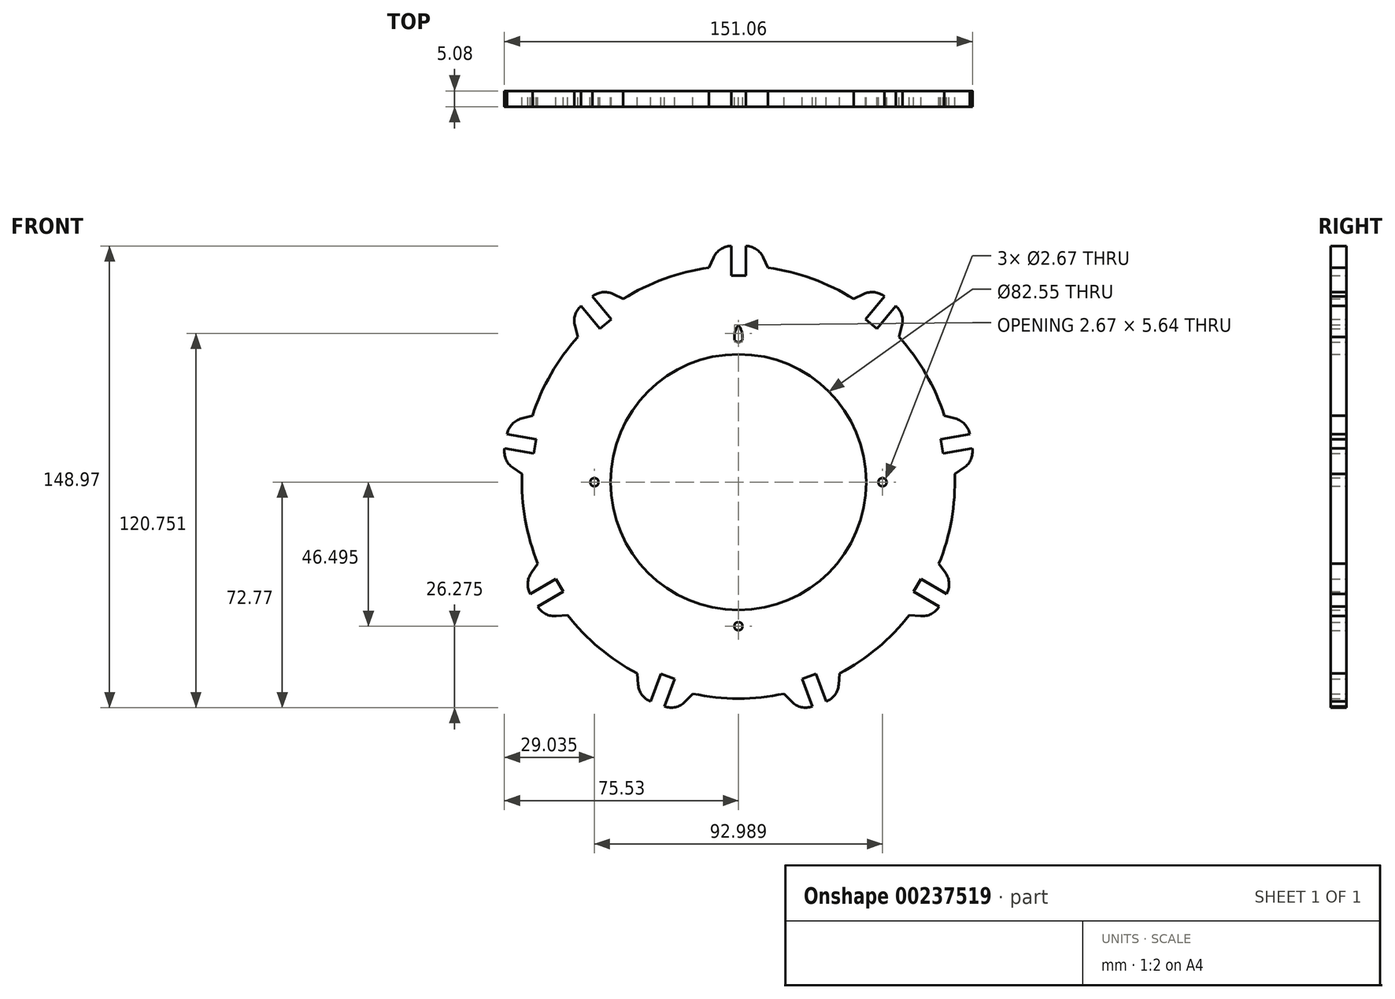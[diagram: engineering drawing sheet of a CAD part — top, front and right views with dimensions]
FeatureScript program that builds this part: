
annotation { "Feature Type Name" : "Feature", "Feature Type Description" : "" }
export const myFeature = defineFeature(function(context is Context, id is Id, definition is map)
    precondition{}
    {
        {
            var Q0;
            Q0=qCreatedBy(makeId("Front.planeOp"),FACE);
            var sketch = newSketch(context, id + "F0", { "sketchPlane" : qUnion([Q0])});
            skCircle(sketch, "E0", {"center": v(0, 0) * mm, "radius": 69.85 * mm});
            skCircle(sketch, "E1", {"center": v(0, 0) * mm, "radius": 41.28 * mm});
            skCircle(sketch, "E2", {"center": v(0, 0) * mm, "radius": 46.5 * mm, "construction": true});
            skPoint(sketch, "E3.center", {"position": v(0, -7.07) * mm});
            skLineSegment(sketch, "E4", {"start": v(-9.56, 69.2) * mm, "end": v(-8.05, 72.5) * mm});
            skLineSegment(sketch, "E5", {"start": v(-2.28, 76.2) * mm, "end": v(2.28, 76.2) * mm});
            skLineSegment(sketch, "E6", {"start": v(8.05, 72.5) * mm, "end": v(9.56, 69.2) * mm});
            skPoint(sketch, "E7", {"position": v(0, 76.2) * mm});
            skLineSegment(sketch, "E8", {"start": v(-9.56, 69.2) * mm, "end": v(-41.28, 0) * mm, "construction": true});
            skLineSegment(sketch, "E9", {"start": v(41.28, 0) * mm, "end": v(9.56, 69.2) * mm, "construction": true});
            skLineSegment(sketch, "E10", {"start": v(-2.35, 76.2) * mm, "end": v(-2.35, 66.67) * mm});
            skLineSegment(sketch, "E11", {"start": v(-2.35, 66.68) * mm, "end": v(2.35, 66.68) * mm});
            skLineSegment(sketch, "E12", {"start": v(2.35, 66.67) * mm, "end": v(2.35, 76.2) * mm});
            skPoint(sketch, "E13", {"position": v(0, 66.67) * mm});
            skPoint(sketch, "E14.visualSharp", {"position": v(-6.35, 76.2) * mm});
            skArc(sketch, "E14.filletArc", {"start": v(-2.28, 76.2) * mm, "mid": v(-5.7, 75.2) * mm, "end": v(-8.05, 72.5) * mm});
            skPoint(sketch, "E15.visualSharp", {"position": v(6.35, 76.2) * mm});
            skArc(sketch, "E15.filletArc", {"start": v(8.05, 72.5) * mm, "mid": v(5.7, 75.2) * mm, "end": v(2.28, 76.2) * mm});
            skCircle(sketch, "E16.MirrorC", {"center": v(0, 46.5) * mm, "radius": 1.33 * mm});
            skCircle(sketch, "E17", {"center": v(0, 0) * mm, "radius": 66.72 * mm, "construction": true});
            skCircle(sketch, "E18.1.0", {"center": v(-46.5, 0) * mm, "radius": 1.33 * mm});
            skCircle(sketch, "E18.2.0", {"center": v(0, -46.5) * mm, "radius": 1.33 * mm});
            skCircle(sketch, "E18.3.0", {"center": v(46.5, 0) * mm, "radius": 1.33 * mm});
            skCircle(sketch, "E19", {"center": v(0, 0) * mm, "radius": 50.8 * mm, "construction": true});
            skArc(sketch, "E20", {"start": v(1.33, 46.48) * mm, "mid": v(1, 48.74) * mm, "end": v(0, 50.8) * mm});
            skArc(sketch, "E21", {"start": v(0, 50.8) * mm, "mid": v(-1, 48.74) * mm, "end": v(-1.33, 46.48) * mm});
            skLineSegment(sketch, "E22.1.0", {"start": v(-51.8, 46.86) * mm, "end": v(-52.76, 50.36) * mm});
            skArc(sketch, "E22.1.1", {"start": v(-50.72, 56.91) * mm, "mid": v(-52.7, 53.94) * mm, "end": v(-52.76, 50.36) * mm});
            skLineSegment(sketch, "E22.1.2", {"start": v(-50.78, 56.86) * mm, "end": v(-44.66, 49.57) * mm});
            skLineSegment(sketch, "E22.1.3", {"start": v(-41.06, 52.59) * mm, "end": v(-47.18, 59.88) * mm});
            skArc(sketch, "E22.1.4", {"start": v(-40.43, 60.7) * mm, "mid": v(-43.96, 61.27) * mm, "end": v(-47.24, 59.84) * mm});
            skLineSegment(sketch, "E22.1.5", {"start": v(-40.43, 60.7) * mm, "end": v(-37.15, 59.15) * mm});
            skLineSegment(sketch, "E22.1.6", {"start": v(-44.66, 49.57) * mm, "end": v(-41.06, 52.59) * mm});
            skLineSegment(sketch, "E22.2.0", {"start": v(-69.8, 2.6) * mm, "end": v(-72.8, 4.66) * mm});
            skArc(sketch, "E22.2.1", {"start": v(-75.44, 11) * mm, "mid": v(-75.04, 7.44) * mm, "end": v(-72.8, 4.66) * mm});
            skLineSegment(sketch, "E22.2.2", {"start": v(-75.45, 10.92) * mm, "end": v(-66.07, 9.26) * mm});
            skLineSegment(sketch, "E22.2.3", {"start": v(-65.25, 13.9) * mm, "end": v(-74.63, 15.55) * mm});
            skArc(sketch, "E22.2.4", {"start": v(-70, 20.51) * mm, "mid": v(-73.06, 18.68) * mm, "end": v(-74.65, 15.47) * mm});
            skLineSegment(sketch, "E22.2.5", {"start": v(-70, 20.51) * mm, "end": v(-66.48, 21.43) * mm});
            skLineSegment(sketch, "E22.2.6", {"start": v(-66.07, 9.26) * mm, "end": v(-65.25, 13.9) * mm});
            skLineSegment(sketch, "E22.3.0", {"start": v(-55.14, -42.88) * mm, "end": v(-58.76, -43.22) * mm});
            skArc(sketch, "E22.3.1", {"start": v(-64.85, -40.07) * mm, "mid": v(-62.27, -42.54) * mm, "end": v(-58.76, -43.22) * mm});
            skLineSegment(sketch, "E22.3.2", {"start": v(-64.82, -40.13) * mm, "end": v(-56.57, -35.37) * mm});
            skLineSegment(sketch, "E22.3.3", {"start": v(-58.92, -31.3) * mm, "end": v(-67.17, -36.07) * mm});
            skArc(sketch, "E22.3.4", {"start": v(-66.8, -29.28) * mm, "mid": v(-67.97, -32.66) * mm, "end": v(-67.13, -36.13) * mm});
            skLineSegment(sketch, "E22.3.5", {"start": v(-66.8, -29.28) * mm, "end": v(-64.7, -26.32) * mm});
            skLineSegment(sketch, "E22.3.6", {"start": v(-56.57, -35.37) * mm, "end": v(-58.92, -31.3) * mm});
            skLineSegment(sketch, "E22.4.0", {"start": v(-14.68, -68.29) * mm, "end": v(-17.23, -70.88) * mm});
            skArc(sketch, "E22.4.1", {"start": v(-23.92, -72.38) * mm, "mid": v(-20.36, -72.61) * mm, "end": v(-17.23, -70.88) * mm});
            skLineSegment(sketch, "E22.4.2", {"start": v(-23.85, -72.4) * mm, "end": v(-20.6, -63.46) * mm});
            skLineSegment(sketch, "E22.4.3", {"start": v(-25.01, -61.85) * mm, "end": v(-28.27, -70.8) * mm});
            skArc(sketch, "E22.4.4", {"start": v(-32.36, -65.37) * mm, "mid": v(-31.08, -68.7) * mm, "end": v(-28.2, -70.83) * mm});
            skLineSegment(sketch, "E22.4.5", {"start": v(-32.36, -65.37) * mm, "end": v(-32.65, -61.75) * mm});
            skLineSegment(sketch, "E22.4.6", {"start": v(-20.6, -63.46) * mm, "end": v(-25.01, -61.85) * mm});
            skLineSegment(sketch, "E22.5.0", {"start": v(32.65, -61.75) * mm, "end": v(32.36, -65.37) * mm});
            skArc(sketch, "E22.5.1", {"start": v(28.2, -70.83) * mm, "mid": v(31.08, -68.7) * mm, "end": v(32.36, -65.37) * mm});
            skLineSegment(sketch, "E22.5.2", {"start": v(28.27, -70.8) * mm, "end": v(25.01, -61.85) * mm});
            skLineSegment(sketch, "E22.5.3", {"start": v(20.6, -63.46) * mm, "end": v(23.85, -72.4) * mm});
            skArc(sketch, "E22.5.4", {"start": v(17.23, -70.88) * mm, "mid": v(20.36, -72.61) * mm, "end": v(23.92, -72.38) * mm});
            skLineSegment(sketch, "E22.5.5", {"start": v(17.23, -70.88) * mm, "end": v(14.68, -68.29) * mm});
            skLineSegment(sketch, "E22.5.6", {"start": v(25.01, -61.85) * mm, "end": v(20.6, -63.46) * mm});
            skLineSegment(sketch, "E22.6.0", {"start": v(64.7, -26.32) * mm, "end": v(66.8, -29.28) * mm});
            skArc(sketch, "E22.6.1", {"start": v(67.13, -36.13) * mm, "mid": v(67.97, -32.66) * mm, "end": v(66.8, -29.28) * mm});
            skLineSegment(sketch, "E22.6.2", {"start": v(67.17, -36.07) * mm, "end": v(58.92, -31.3) * mm});
            skLineSegment(sketch, "E22.6.3", {"start": v(56.57, -35.37) * mm, "end": v(64.82, -40.13) * mm});
            skArc(sketch, "E22.6.4", {"start": v(58.76, -43.22) * mm, "mid": v(62.27, -42.54) * mm, "end": v(64.85, -40.07) * mm});
            skLineSegment(sketch, "E22.6.5", {"start": v(58.76, -43.22) * mm, "end": v(55.14, -42.88) * mm});
            skLineSegment(sketch, "E22.6.6", {"start": v(58.92, -31.3) * mm, "end": v(56.57, -35.37) * mm});
            skLineSegment(sketch, "E22.7.0", {"start": v(66.48, 21.43) * mm, "end": v(70, 20.51) * mm});
            skArc(sketch, "E22.7.1", {"start": v(74.65, 15.47) * mm, "mid": v(73.06, 18.68) * mm, "end": v(70, 20.51) * mm});
            skLineSegment(sketch, "E22.7.2", {"start": v(74.63, 15.55) * mm, "end": v(65.25, 13.9) * mm});
            skLineSegment(sketch, "E22.7.3", {"start": v(66.07, 9.26) * mm, "end": v(75.45, 10.92) * mm});
            skArc(sketch, "E22.7.4", {"start": v(72.8, 4.66) * mm, "mid": v(75.04, 7.44) * mm, "end": v(75.44, 11) * mm});
            skLineSegment(sketch, "E22.7.5", {"start": v(72.8, 4.66) * mm, "end": v(69.8, 2.6) * mm});
            skLineSegment(sketch, "E22.7.6", {"start": v(65.25, 13.9) * mm, "end": v(66.07, 9.26) * mm});
            skLineSegment(sketch, "E22.8.0", {"start": v(37.15, 59.15) * mm, "end": v(40.43, 60.7) * mm});
            skArc(sketch, "E22.8.1", {"start": v(47.24, 59.84) * mm, "mid": v(43.96, 61.27) * mm, "end": v(40.43, 60.7) * mm});
            skLineSegment(sketch, "E22.8.2", {"start": v(47.18, 59.88) * mm, "end": v(41.06, 52.59) * mm});
            skLineSegment(sketch, "E22.8.3", {"start": v(44.66, 49.57) * mm, "end": v(50.78, 56.86) * mm});
            skArc(sketch, "E22.8.4", {"start": v(52.76, 50.36) * mm, "mid": v(52.7, 53.94) * mm, "end": v(50.72, 56.91) * mm});
            skLineSegment(sketch, "E22.8.5", {"start": v(52.76, 50.36) * mm, "end": v(51.8, 46.86) * mm});
            skLineSegment(sketch, "E22.8.6", {"start": v(41.06, 52.59) * mm, "end": v(44.66, 49.57) * mm});
            skSolve(sketch);
        }
        {
            var Q0;
            Q0=makeQuery(id+"F0.imprint","IMPRINT",FACE,{"disambiguationData":[TD([[makeQuery(id+"F0.imprint","IMPRINT",EDGE,{"derivedFrom":sQuery(id+"F0.wireOp",EDGE,"E1")}),-1.0]])]});
            var Q1;
            {var subQ0=sQuery(id+"F0.wireOp",EDGE,"E22.1.5");Q1=makeQuery(id+"F0.imprint","IMPRINT",FACE,{"disambiguationData":[TD([[makeQuery(id+"F0.imprint","IMPRINT",EDGE,{"derivedFrom":subQ0}),-1.0]])]});}
            var Q2;
            {var subQ0=sQuery(id+"F0.wireOp",EDGE,"E22.1.0");Q2=makeQuery(id+"F0.imprint","IMPRINT",FACE,{"disambiguationData":[TD([[makeQuery(id+"F0.imprint","IMPRINT",EDGE,{"derivedFrom":subQ0}),-1.0]])]});}
            var Q3;
            {var subQ0=sQuery(id+"F0.wireOp",EDGE,"E4");Q3=makeQuery(id+"F0.imprint","IMPRINT",FACE,{"disambiguationData":[TD([[makeQuery(id+"F0.imprint","IMPRINT",EDGE,{"derivedFrom":subQ0}),-1.0]])]});}
            var Q4;
            {var subQ0=sQuery(id+"F0.wireOp",EDGE,"E6");Q4=makeQuery(id+"F0.imprint","IMPRINT",FACE,{"disambiguationData":[TD([[makeQuery(id+"F0.imprint","IMPRINT",EDGE,{"derivedFrom":subQ0}),-1.0]])]});}
            var Q5;
            {var subQ0=sQuery(id+"F0.wireOp",EDGE,"E22.8.0");Q5=makeQuery(id+"F0.imprint","IMPRINT",FACE,{"disambiguationData":[TD([[makeQuery(id+"F0.imprint","IMPRINT",EDGE,{"derivedFrom":subQ0}),-1.0]])]});}
            var Q6;
            {var subQ0=sQuery(id+"F0.wireOp",EDGE,"E22.8.5");Q6=makeQuery(id+"F0.imprint","IMPRINT",FACE,{"disambiguationData":[TD([[makeQuery(id+"F0.imprint","IMPRINT",EDGE,{"derivedFrom":subQ0}),-1.0]])]});}
            var Q7;
            {var subQ0=sQuery(id+"F0.wireOp",EDGE,"E22.7.0");Q7=makeQuery(id+"F0.imprint","IMPRINT",FACE,{"disambiguationData":[TD([[makeQuery(id+"F0.imprint","IMPRINT",EDGE,{"derivedFrom":subQ0}),-1.0]])]});}
            var Q8;
            {var subQ0=sQuery(id+"F0.wireOp",EDGE,"E22.7.5");Q8=makeQuery(id+"F0.imprint","IMPRINT",FACE,{"disambiguationData":[TD([[makeQuery(id+"F0.imprint","IMPRINT",EDGE,{"derivedFrom":subQ0}),-1.0]])]});}
            var Q9;
            {var subQ0=sQuery(id+"F0.wireOp",EDGE,"E22.6.0");Q9=makeQuery(id+"F0.imprint","IMPRINT",FACE,{"disambiguationData":[TD([[makeQuery(id+"F0.imprint","IMPRINT",EDGE,{"derivedFrom":subQ0}),-1.0]])]});}
            var Q10;
            {var subQ0=sQuery(id+"F0.wireOp",EDGE,"E22.6.5");Q10=makeQuery(id+"F0.imprint","IMPRINT",FACE,{"disambiguationData":[TD([[makeQuery(id+"F0.imprint","IMPRINT",EDGE,{"derivedFrom":subQ0}),-1.0]])]});}
            var Q11;
            {var subQ0=sQuery(id+"F0.wireOp",EDGE,"E22.5.5");Q11=makeQuery(id+"F0.imprint","IMPRINT",FACE,{"disambiguationData":[TD([[makeQuery(id+"F0.imprint","IMPRINT",EDGE,{"derivedFrom":subQ0}),-1.0]])]});}
            var Q12;
            {var subQ0=sQuery(id+"F0.wireOp",EDGE,"E22.5.0");Q12=makeQuery(id+"F0.imprint","IMPRINT",FACE,{"disambiguationData":[TD([[makeQuery(id+"F0.imprint","IMPRINT",EDGE,{"derivedFrom":subQ0}),-1.0]])]});}
            var Q13;
            {var subQ0=sQuery(id+"F0.wireOp",EDGE,"E22.4.5");Q13=makeQuery(id+"F0.imprint","IMPRINT",FACE,{"disambiguationData":[TD([[makeQuery(id+"F0.imprint","IMPRINT",EDGE,{"derivedFrom":subQ0}),-1.0]])]});}
            var Q14;
            {var subQ0=sQuery(id+"F0.wireOp",EDGE,"E22.4.0");Q14=makeQuery(id+"F0.imprint","IMPRINT",FACE,{"disambiguationData":[TD([[makeQuery(id+"F0.imprint","IMPRINT",EDGE,{"derivedFrom":subQ0}),-1.0]])]});}
            var Q15;
            {var subQ0=sQuery(id+"F0.wireOp",EDGE,"E22.3.0");Q15=makeQuery(id+"F0.imprint","IMPRINT",FACE,{"disambiguationData":[TD([[makeQuery(id+"F0.imprint","IMPRINT",EDGE,{"derivedFrom":subQ0}),-1.0]])]});}
            var Q16;
            {var subQ0=sQuery(id+"F0.wireOp",EDGE,"E22.3.5");Q16=makeQuery(id+"F0.imprint","IMPRINT",FACE,{"disambiguationData":[TD([[makeQuery(id+"F0.imprint","IMPRINT",EDGE,{"derivedFrom":subQ0}),-1.0]])]});}
            var Q17;
            {var subQ0=sQuery(id+"F0.wireOp",EDGE,"E22.2.0");Q17=makeQuery(id+"F0.imprint","IMPRINT",FACE,{"disambiguationData":[TD([[makeQuery(id+"F0.imprint","IMPRINT",EDGE,{"derivedFrom":subQ0}),-1.0]])]});}
            var Q18;
            {var subQ0=sQuery(id+"F0.wireOp",EDGE,"E22.2.5");Q18=makeQuery(id+"F0.imprint","IMPRINT",FACE,{"disambiguationData":[TD([[makeQuery(id+"F0.imprint","IMPRINT",EDGE,{"derivedFrom":subQ0}),-1.0]])]});}
            extrude(context, id + "F1", {"entities" : qUnion([Q0, Q1, Q2, Q3, Q4, Q5, Q6, Q7, Q8, Q9, Q10, Q11, Q12, Q13, Q14, Q15, Q16, Q17, Q18]), "depth" : 5.08 * mm});
        }
    });
